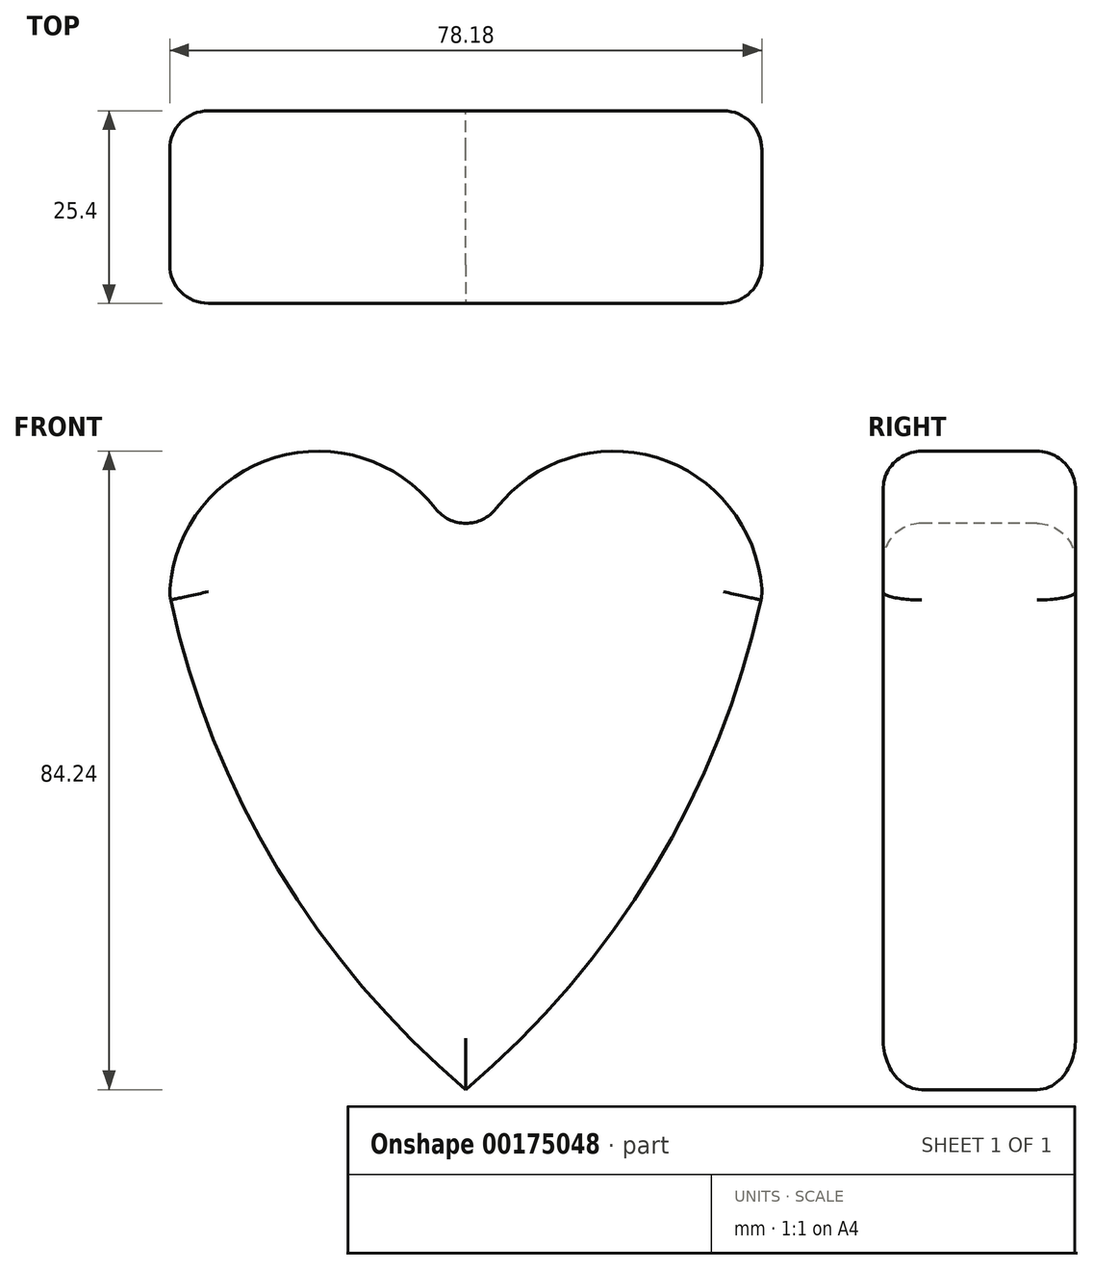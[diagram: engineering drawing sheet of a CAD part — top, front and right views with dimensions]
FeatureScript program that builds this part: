
annotation { "Feature Type Name" : "Feature", "Feature Type Description" : "" }
export const myFeature = defineFeature(function(context is Context, id is Id, definition is map)
    precondition{}
    {
        {
            var Q0;
            Q0=qCreatedBy(makeId("Front.planeOp"),FACE);
            var sketch = newSketch(context, id + "F0", { "sketchPlane" : qUnion([Q0])});
            skArc(sketch, "E0", {"start": v(0, 24.38) * mm, "mid": v(-17.97, 46.33) * mm, "end": v(-39.12, 27.43) * mm});
            skArc(sketch, "E1", {"start": v(-39.12, 27.43) * mm, "mid": v(-25, -8.46) * mm, "end": v(0, -37.85) * mm});
            skArc(sketch, "E2.MirrorCS", {"start": v(0, 24.38) * mm, "mid": v(17.97, 46.33) * mm, "end": v(39.12, 27.43) * mm});
            skArc(sketch, "E3.MirrorCS", {"start": v(39.12, 27.43) * mm, "mid": v(25, -8.46) * mm, "end": v(0, -37.85) * mm});
            skSolve(sketch);
        }
        {
            var Q0;
            Q0 = qSketchRegion(id + "F0", true);
            extrude(context, id + "F1", {"entities" : qUnion([Q0]), "depth" : 25.4 * mm, "offsetDistance" : 25.4 * mm});
        }
        {
            var Q0;
            Q0=makeQuery(id+"F1.opExtrude","CAP_EDGE",EDGE,{"disambiguationData":[OSD([sQuery(id+"F0.wireOp",EDGE,"E1")])],"isStart":false});
            var Q1;
            Q1=makeQuery(id+"F1.opExtrude","CAP_EDGE",EDGE,{"disambiguationData":[OSD([sQuery(id+"F0.wireOp",EDGE,"E3.MirrorCS")])],"isStart":false});
            var Q2;
            Q2=makeQuery(id+"F1.opExtrude","CAP_EDGE",EDGE,{"disambiguationData":[OSD([sQuery(id+"F0.wireOp",EDGE,"E1")])],"isStart":true});
            var Q3;
            Q3=makeQuery(id+"F1.opExtrude","CAP_EDGE",EDGE,{"disambiguationData":[OSD([sQuery(id+"F0.wireOp",EDGE,"E3.MirrorCS")])],"isStart":true});
            fillet(context, id + "F2", {"entities" : qUnion([Q0, Q1, Q2, Q3]), "radius" : 5.08 * mm, "allowEdgeOverflow" : false});
        }
        {
            var Q0;
            Q0=makeQuery(id+"F1.opExtrude","CAP_EDGE",EDGE,{"disambiguationData":[OSD([sQuery(id+"F0.wireOp",EDGE,"E2.MirrorCS")])],"isStart":true});
            var Q1;
            Q1=makeQuery(id+"F2.opFillet","BLEND_EDGE",EDGE,{"blendedFrom":[makeQuery(id+"F1.opExtrude","CAP_EDGE",EDGE,{"disambiguationData":[OSD([sQuery(id+"F0.wireOp",EDGE,"E3.MirrorCS")])],"isStart":true}),makeQuery(id+"F1.opExtrude","SWEPT_FACE",FACE,{"disambiguationData":[OSD([sQuery(id+"F0.wireOp",EDGE,"E2.MirrorCS")])]})],"blendedInto":[makeQuery(id+"F1.opExtrude","SWEPT_FACE",FACE,{"disambiguationData":[OSD([sQuery(id+"F0.wireOp",EDGE,"E2.MirrorCS")])]})]});
            var Q2;
            Q2=makeQuery(id+"F1.opExtrude","CAP_EDGE",EDGE,{"disambiguationData":[OSD([sQuery(id+"F0.wireOp",EDGE,"E2.MirrorCS")])],"isStart":false});
            var Q3;
            Q3=makeQuery(id+"F1.opExtrude","SWEPT_FACE",FACE,{"disambiguationData":[OSD([sQuery(id+"F0.wireOp",EDGE,"E0")])]});
            fillet(context, id + "F3", {"entities" : qUnion([Q0, Q1, Q2, Q3]), "radius" : 5.08 * mm, "tangentPropagation" : true, "allowEdgeOverflow" : false});
        }
    });
